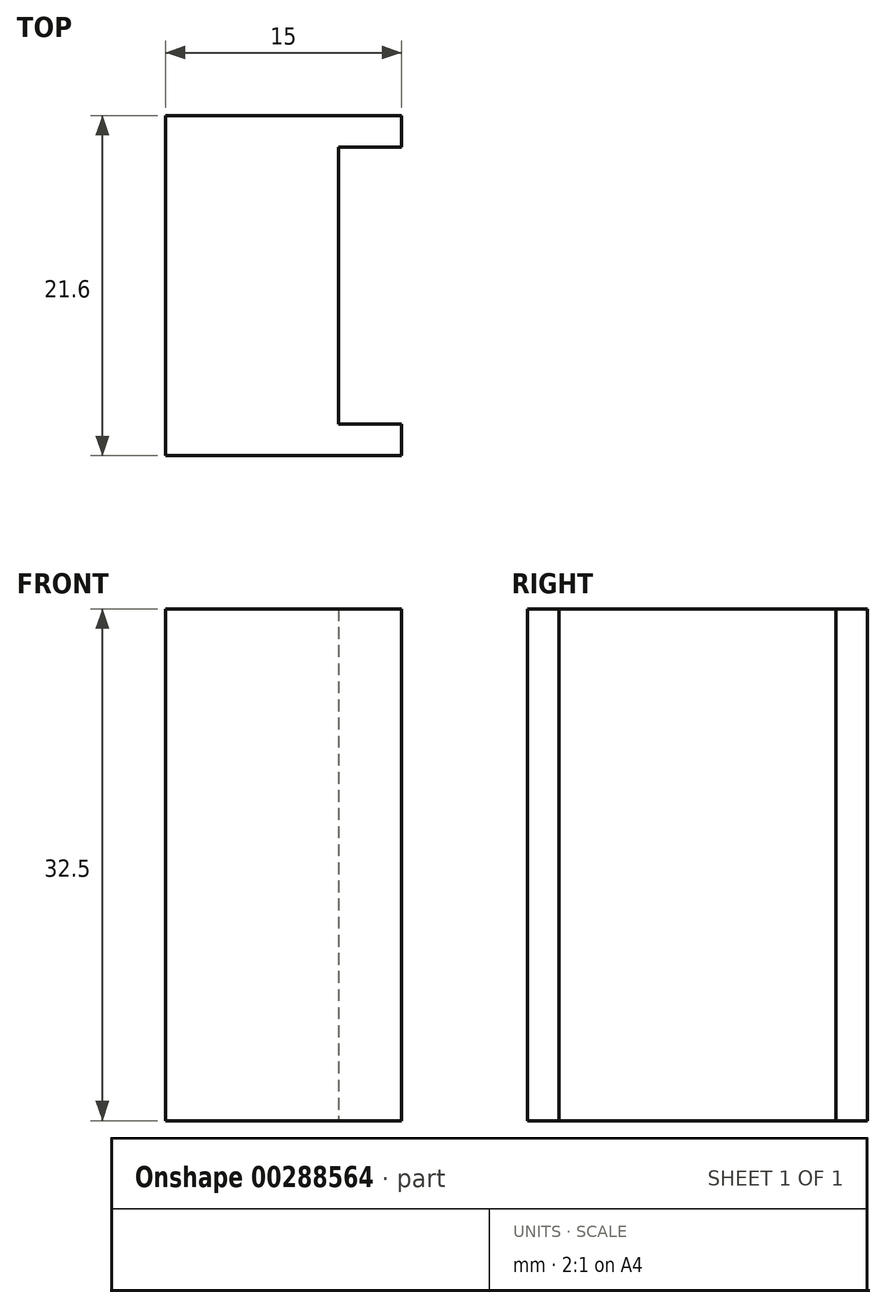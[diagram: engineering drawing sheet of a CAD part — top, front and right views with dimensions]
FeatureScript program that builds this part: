
annotation { "Feature Type Name" : "Feature", "Feature Type Description" : "" }
export const myFeature = defineFeature(function(context is Context, id is Id, definition is map)
    precondition{}
    {
        {
            var Q0;
            Q0=qCreatedBy(makeId("Top.planeOp"),FACE);
            var sketch = newSketch(context, id + "F0", { "sketchPlane" : qUnion([Q0])});
            skLineSegment(sketch, "E0.bottom", {"start": v(5.5, 10.8) * mm, "end": v(-5.5, 10.8) * mm});
            skLineSegment(sketch, "E0.top", {"start": v(5.5, -10.8) * mm, "end": v(-5.5, -10.8) * mm});
            skLineSegment(sketch, "E0.left", {"start": v(5.5, 10.8) * mm, "end": v(5.5, -10.8) * mm});
            skLineSegment(sketch, "E0.right", {"start": v(-5.5, 10.8) * mm, "end": v(-5.5, -10.8) * mm});
            skPoint(sketch, "E0.middle", {"position": v(0, 0) * mm});
            skLineSegment(sketch, "E1.bottom", {"start": v(5.5, 10.8) * mm, "end": v(9.5, 10.8) * mm});
            skLineSegment(sketch, "E1.top", {"start": v(5.5, 8.8) * mm, "end": v(9.5, 8.8) * mm});
            skLineSegment(sketch, "E1.left", {"start": v(5.5, 10.8) * mm, "end": v(5.5, 8.8) * mm});
            skLineSegment(sketch, "E1.right", {"start": v(9.5, 10.8) * mm, "end": v(9.5, 8.8) * mm});
            skLineSegment(sketch, "E2.MirrorCS", {"start": v(5.5, -8.8) * mm, "end": v(9.5, -8.8) * mm});
            skLineSegment(sketch, "E3.MirrorCS", {"start": v(5.5, -10.8) * mm, "end": v(9.5, -10.8) * mm});
            skLineSegment(sketch, "E4.MirrorCS", {"start": v(9.5, -10.8) * mm, "end": v(9.5, -8.8) * mm});
            skSolve(sketch);
        }
        {
            var Q0;
            {var subQ1=sQuery(id+"F0.wireOp",EDGE,"E0.bottom");Q0=makeQuery(id+"F0.imprint","IMPRINT",FACE,{"disambiguationData":[TD([[makeQuery(id+"F0.imprint","IMPRINT",EDGE,{"derivedFrom":subQ1}),1.0]])]});}
            var Q1;
            {var subQ0=sQuery(id+"F0.wireOp",EDGE,"E1.bottom");Q1=makeQuery(id+"F0.imprint","IMPRINT",FACE,{"disambiguationData":[TD([[makeQuery(id+"F0.imprint","IMPRINT",EDGE,{"derivedFrom":subQ0}),-1.0]])]});}
            var Q2;
            {var subQ2=sQuery(id+"F0.wireOp",EDGE,"E2.MirrorCS");Q2=makeQuery(id+"F0.imprint","IMPRINT",FACE,{"disambiguationData":[TD([[makeQuery(id+"F0.imprint","IMPRINT",EDGE,{"derivedFrom":subQ2}),-1.0]])]});}
            extrude(context, id + "F1", {"entities" : qUnion([Q0, Q1, Q2]), "depth" : 32.5 * mm, "offsetDistance" : 25 * mm});
        }
    });
